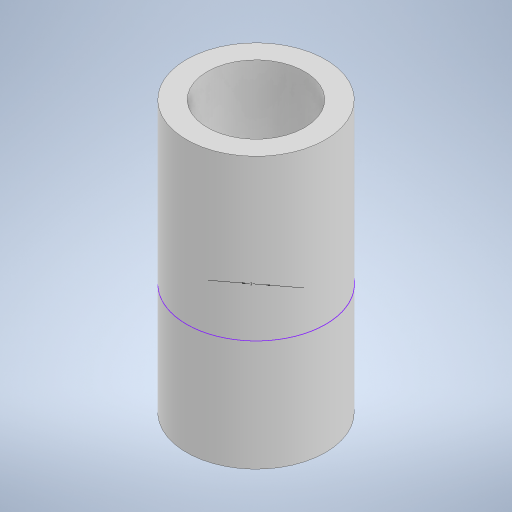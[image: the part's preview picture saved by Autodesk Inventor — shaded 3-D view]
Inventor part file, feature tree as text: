
AUTODESK INVENTOR PART (.ipt)
format: ipt  version: 2024 (Build 280153000, 153)  size: 255,488 bytes
history: native  units: mm
features: sketch x4, extrude x2, revolve x1
ambient origin geometry x8: Origin, YZ Plane, XZ Plane, XY Plane, X Axis, Y Axis, Z Axis, Center Point
bodies: Solid1 (feature_tree)
feature tree (7):
  extrude  "Extrusion1"  Depth=10.0mm
  sketch  "Sketch2"  dims[d2=8.0mm d3=0.0mm d4=1.0mm]
  revolve  "Revolution1"  [1 undecoded]
  extrude  "Extrusion2"  Depth=3.5mm
  sketch  "Sketch1"  dims[d0=3.1mm d1=10.0mm]
  sketch  "Sketch5"  dims[d20=3.5mm d21=1.5mm]
  sketch  "Sketch7"  dims[d22=4.5mm d23=3.0mm d24=90.0deg d25=8.0mm d26=0.0mm d27=0.15mm d28=60.0mm d30=360.0deg]
note: 1 required parameter value undecoded (feature->parameter linkage not recoverable at this tier; creation-order binding heuristic only, values carry confidence <= 0.55)
